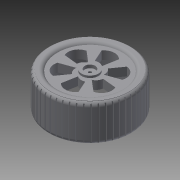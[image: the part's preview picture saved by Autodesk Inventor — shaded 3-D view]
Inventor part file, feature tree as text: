
AUTODESK INVENTOR PART (.ipt)
format: ipt  version: 2015 (Build 190159000, 159)  size: 542,720 bytes
history: native  units: mm
features: sketch x8, extrude x5, fillet x3, hole x2, pattern_circular x2, revolve x1, projected_geometry x1
ambient origin geometry x8: Origin, YZ Plane, XZ Plane, XY Plane, X Axis, Y Axis, Z Axis, Center Point
bodies: Solid1 (feature_tree)
feature tree (22):
  revolve  "Revolution1"  [1 undecoded]
  fillet  "Fillet1"  Radius=35.0mm
  extrude  "Extrusion1"  Depth=4.0mm
  fillet  "Fillet2"  Radius=75.0mm
  hole  "Hole1"  [1 undecoded]
  extrude  "Extrusion2"  Depth=10.0mm TaperAngle=0.0deg
  extrude  "Extrusion3"  Depth=4.0mm
  fillet  "Fillet3"  Radius=60.0mm
  pattern_circular  "Circular Pattern1"  [2 undecoded]
  hole  "Hole2"  [1 undecoded]
  extrude  "Extrusion4"  Depth=10.0mm
  pattern_circular  "Circular Pattern2"  [2 undecoded]
  extrude  "Extrusion5"  [1 undecoded]
  sketch  "Sketch1"  dims[d2=5.0mm d3=35.0mm d4=35.0mm]
  sketch  "Sketch2"  dims[d5=90.0deg d6=4.0mm d7=75.0mm]
  sketch  "Sketch3"  dims[d8=10.0mm d9=0.0mm d10=4.0mm]
  sketch  "Sketch4"  dims[d11=3.0mm d12=6.0mm d13=10.0mm d14=3.0mm d15=90.0deg d16=8.0mm d17=20.594885mm d18=10.0mm d19=0.0mm]
  sketch  "Sketch5"  dims[d20=2.0mm d21=0.0mm d22=4.0mm d23=60.0mm d24=360.0deg]
  sketch  "Sketch6"  dims[d26=10.0mm d27=6.0mm d28=10.0mm d29=3.0mm d30=90.0deg d31=2.0mm d32=0.0mm]
  sketch  "Sketch7"  dims[d33=1.0mm]
  sketch  "Sketch8"  dims[d34=1.0mm d35=10.0mm d36=0.0mm d37=500.0mm d38=360.0deg d40=16.0mm d41=2.0mm d42=0.0mm]
  projected_geometry  "Projected Loop1"
note: 8 required parameter values undecoded (feature->parameter linkage not recoverable at this tier; creation-order binding heuristic only, values carry confidence <= 0.55)